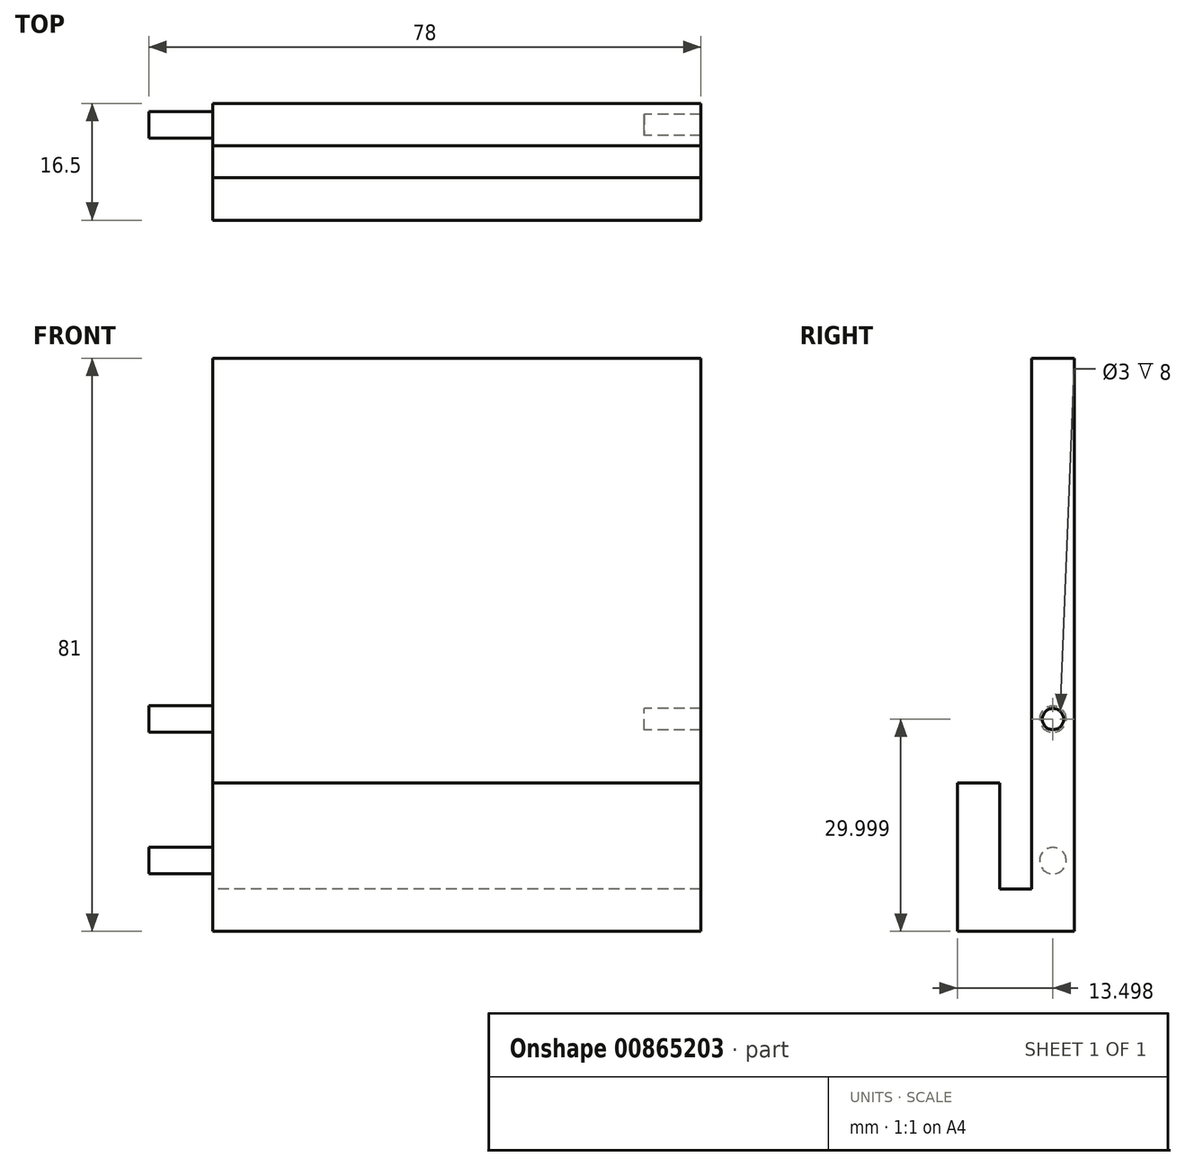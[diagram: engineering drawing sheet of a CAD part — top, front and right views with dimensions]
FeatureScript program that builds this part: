
annotation { "Feature Type Name" : "Feature", "Feature Type Description" : "" }
export const myFeature = defineFeature(function(context is Context, id is Id, definition is map)
    precondition{}
    {
        {
            var Q0;
            Q0=qCreatedBy(makeId("Right.planeOp"),FACE);
            var sketch = newSketch(context, id + "F0", { "sketchPlane" : qUnion([Q0])});
            skLineSegment(sketch, "E0", {"start": v(15.98, 53.88) * mm, "end": v(15.98, -27.12) * mm});
            skLineSegment(sketch, "E1", {"start": v(-0.52, -27.12) * mm, "end": v(15.98, -27.12) * mm});
            skLineSegment(sketch, "E2", {"start": v(-0.52, -27.12) * mm, "end": v(-0.52, -6.12) * mm});
            skLineSegment(sketch, "E3", {"start": v(5.48, -6.12) * mm, "end": v(5.48, -21.12) * mm});
            skLineSegment(sketch, "E4", {"start": v(5.48, -21.12) * mm, "end": v(9.98, -21.12) * mm});
            skLineSegment(sketch, "E5", {"start": v(9.98, -21.12) * mm, "end": v(9.98, 53.88) * mm});
            skLineSegment(sketch, "E6", {"start": v(9.98, 53.88) * mm, "end": v(15.98, 53.88) * mm});
            skLineSegment(sketch, "E7", {"start": v(-0.52, -6.12) * mm, "end": v(5.48, -6.12) * mm});
            skSolve(sketch);
        }
        {
            var Q0;
            Q0=makeQuery(id+"F0.imprint","IMPRINT",FACE,{"disambiguationData":[TD([[makeQuery(id+"F0.imprint","IMPRINT",EDGE,{"derivedFrom":sQuery(id+"F0.wireOp",EDGE,"E0")}),-1.0]])]});
            extrude(context, id + "F1", {"entities" : qUnion([Q0]), "depth" : 70 * mm, "offsetDistance" : 25 * mm});
        }
        {
            var Q0;
            Q0=makeQuery(id+"F1.opExtrude","CAP_FACE",FACE,{"disambiguationData":[OSD([sQuery(id+"F0.wireOp",EDGE,"E0"),sQuery(id+"F0.wireOp",EDGE,"E1"),sQuery(id+"F0.wireOp",EDGE,"E2"),sQuery(id+"F0.wireOp",EDGE,"E3"),sQuery(id+"F0.wireOp",EDGE,"E4"),sQuery(id+"F0.wireOp",EDGE,"E5"),sQuery(id+"F0.wireOp",EDGE,"E6"),sQuery(id+"F0.wireOp",EDGE,"E7")])],"isStart":false});
            var sketch = newSketch(context, id + "F2", { "sketchPlane" : qUnion([Q0])});
            skCircle(sketch, "E8", {"center": v(12.98, 43.88) * mm, "radius": 1.5 * mm});
            skCircle(sketch, "E9", {"center": v(12.98, 23.88) * mm, "radius": 1.5 * mm});
            skCircle(sketch, "E10.MirrorC", {"center": v(12.98, 2.88) * mm, "radius": 1.5 * mm});
            skLineSegment(sketch, "E11", {"start": v(12.98, 43.88) * mm, "end": v(12.98, 53.88) * mm});
            skLineSegment(sketch, "E12", {"start": v(12.98, 43.88) * mm, "end": v(12.98, 23.88) * mm});
            skLineSegment(sketch, "E13", {"start": v(12.98, 23.88) * mm, "end": v(12.98, 2.88) * mm});
            skLineSegment(sketch, "E14", {"start": v(12.98, 2.88) * mm, "end": v(12.98, -17.12) * mm});
            skCircle(sketch, "E15", {"center": v(12.98, -17.12) * mm, "radius": 1.5 * mm});
            skSolve(sketch);
        }
        {
            var Q0;
            {var subQ0=sQuery(id+"F2.wireOp",EDGE,"E11");var subQ1=sQuery(id+"F2.wireOp",EDGE,"E8");var subQ2=makeQuery(id+"F2.imprint","INTERSECT",VERTEX,{"derivedFrom":[subQ1,subQ0]});Q0=makeQuery(id+"F2.imprint","IMPRINT",FACE,{"disambiguationData":[TD([[makeQuery(id+"F2.imprint","IMPRINT",EDGE,{"disambiguationData":[TD([[subQ2,1.0]])],"derivedFrom":subQ1}),1.0]])]});}
            var Q1;
            {var subQ0=sQuery(id+"F2.wireOp",EDGE,"E11");var subQ1=sQuery(id+"F2.wireOp",EDGE,"E8");var subQ2=makeQuery(id+"F2.imprint","INTERSECT",VERTEX,{"derivedFrom":[subQ1,subQ0]});Q1=makeQuery(id+"F2.imprint","IMPRINT",FACE,{"disambiguationData":[TD([[makeQuery(id+"F2.imprint","IMPRINT",EDGE,{"disambiguationData":[TD([[subQ2,-1.0]])],"derivedFrom":subQ1}),1.0]])]});}
            var Q2;
            {var subQ0=sQuery(id+"F2.wireOp",EDGE,"E12");var subQ1=sQuery(id+"F2.wireOp",EDGE,"E9");var subQ2=makeQuery(id+"F2.imprint","INTERSECT",VERTEX,{"derivedFrom":[subQ1,subQ0]});Q2=makeQuery(id+"F2.imprint","IMPRINT",FACE,{"disambiguationData":[TD([[makeQuery(id+"F2.imprint","IMPRINT",EDGE,{"disambiguationData":[TD([[subQ2,1.0]])],"derivedFrom":subQ1}),1.0]])]});}
            var Q3;
            {var subQ0=sQuery(id+"F2.wireOp",EDGE,"E12");var subQ1=sQuery(id+"F2.wireOp",EDGE,"E9");var subQ2=makeQuery(id+"F2.imprint","INTERSECT",VERTEX,{"derivedFrom":[subQ1,subQ0]});Q3=makeQuery(id+"F2.imprint","IMPRINT",FACE,{"disambiguationData":[TD([[makeQuery(id+"F2.imprint","IMPRINT",EDGE,{"disambiguationData":[TD([[subQ2,-1.0]])],"derivedFrom":subQ1}),1.0]])]});}
            var Q4;
            {var subQ0=sQuery(id+"F2.wireOp",EDGE,"E13");var subQ1=sQuery(id+"F2.wireOp",EDGE,"E10.MirrorC");var subQ2=makeQuery(id+"F2.imprint","INTERSECT",VERTEX,{"derivedFrom":[subQ1,subQ0]});Q4=makeQuery(id+"F2.imprint","IMPRINT",FACE,{"disambiguationData":[TD([[makeQuery(id+"F2.imprint","IMPRINT",EDGE,{"disambiguationData":[TD([[subQ2,-1.0]])],"derivedFrom":subQ1}),-1.0]])]});}
            var Q5;
            {var subQ0=sQuery(id+"F2.wireOp",EDGE,"E13");var subQ1=sQuery(id+"F2.wireOp",EDGE,"E10.MirrorC");var subQ2=makeQuery(id+"F2.imprint","INTERSECT",VERTEX,{"derivedFrom":[subQ1,subQ0]});Q5=makeQuery(id+"F2.imprint","IMPRINT",FACE,{"disambiguationData":[TD([[makeQuery(id+"F2.imprint","IMPRINT",EDGE,{"disambiguationData":[TD([[subQ2,1.0]])],"derivedFrom":subQ1}),-1.0]])]});}
            var Q6;
            Q6=makeQuery(id+"F2.imprint","IMPRINT",FACE,{"disambiguationData":[TD([[makeQuery(id+"F2.imprint","IMPRINT",EDGE,{"derivedFrom":sQuery(id+"F2.wireOp",EDGE,"E15")}),1.0]])]});
            extrude(context, id + "F3", {"entities" : qUnion([Q0, Q1, Q2, Q3, Q4, Q5, Q6]), "operationType" : NewBodyOperationType.ADD, "depth" : 8 * mm, "offsetDistance" : 25 * mm});
        }
        {
            var Q0;
            Q0=makeQuery(id+"F1.opExtrude","CAP_FACE",FACE,{"disambiguationData":[OSD([sQuery(id+"F0.wireOp",EDGE,"E0"),sQuery(id+"F0.wireOp",EDGE,"E1"),sQuery(id+"F0.wireOp",EDGE,"E2"),sQuery(id+"F0.wireOp",EDGE,"E3"),sQuery(id+"F0.wireOp",EDGE,"E4"),sQuery(id+"F0.wireOp",EDGE,"E5"),sQuery(id+"F0.wireOp",EDGE,"E6"),sQuery(id+"F0.wireOp",EDGE,"E7")])],"isStart":true});
            var sketch = newSketch(context, id + "F4", { "sketchPlane" : qUnion([Q0])});
            skCircle(sketch, "E16", {"center": v(-12.98, 43.88) * mm, "radius": 1.88 * mm});
            skCircle(sketch, "E17", {"center": v(-12.98, 23.88) * mm, "radius": 1.88 * mm});
            skCircle(sketch, "E18.MirrorC", {"center": v(-12.98, -17.12) * mm, "radius": 1.88 * mm});
            skCircle(sketch, "E19.MirrorC", {"center": v(-12.98, 2.88) * mm, "radius": 1.88 * mm});
            skLineSegment(sketch, "E20", {"start": v(-12.98, 53.88) * mm, "end": v(-12.98, 43.88) * mm});
            skLineSegment(sketch, "E21", {"start": v(-12.98, 43.88) * mm, "end": v(-12.98, 23.88) * mm});
            skLineSegment(sketch, "E22", {"start": v(-12.98, 23.88) * mm, "end": v(-12.98, 2.88) * mm});
            skLineSegment(sketch, "E23", {"start": v(-12.98, 2.88) * mm, "end": v(-12.98, -17.12) * mm});
            skLineSegment(sketch, "E24", {"start": v(-12.98, -17.12) * mm, "end": v(-12.98, -27.12) * mm});
            skSolve(sketch);
        }
        {
            var Q0;
            {var subQ0=sQuery(id+"F4.wireOp",EDGE,"E20");var subQ1=sQuery(id+"F4.wireOp",EDGE,"E16");var subQ2=makeQuery(id+"F4.imprint","INTERSECT",VERTEX,{"derivedFrom":[subQ1,subQ0]});Q0=makeQuery(id+"F4.imprint","IMPRINT",FACE,{"disambiguationData":[TD([[makeQuery(id+"F4.imprint","IMPRINT",EDGE,{"disambiguationData":[TD([[subQ2,1.0]])],"derivedFrom":subQ1}),1.0]])]});}
            var Q1;
            {var subQ0=sQuery(id+"F4.wireOp",EDGE,"E20");var subQ1=sQuery(id+"F4.wireOp",EDGE,"E16");var subQ2=makeQuery(id+"F4.imprint","INTERSECT",VERTEX,{"derivedFrom":[subQ1,subQ0]});Q1=makeQuery(id+"F4.imprint","IMPRINT",FACE,{"disambiguationData":[TD([[makeQuery(id+"F4.imprint","IMPRINT",EDGE,{"disambiguationData":[TD([[subQ2,-1.0]])],"derivedFrom":subQ1}),1.0]])]});}
            var Q2;
            {var subQ0=sQuery(id+"F4.wireOp",EDGE,"E21");var subQ1=sQuery(id+"F4.wireOp",EDGE,"E17");var subQ2=makeQuery(id+"F4.imprint","INTERSECT",VERTEX,{"derivedFrom":[subQ1,subQ0]});Q2=makeQuery(id+"F4.imprint","IMPRINT",FACE,{"disambiguationData":[TD([[makeQuery(id+"F4.imprint","IMPRINT",EDGE,{"disambiguationData":[TD([[subQ2,1.0]])],"derivedFrom":subQ1}),1.0]])]});}
            var Q3;
            {var subQ0=sQuery(id+"F4.wireOp",EDGE,"E21");var subQ1=sQuery(id+"F4.wireOp",EDGE,"E17");var subQ2=makeQuery(id+"F4.imprint","INTERSECT",VERTEX,{"derivedFrom":[subQ1,subQ0]});Q3=makeQuery(id+"F4.imprint","IMPRINT",FACE,{"disambiguationData":[TD([[makeQuery(id+"F4.imprint","IMPRINT",EDGE,{"disambiguationData":[TD([[subQ2,-1.0]])],"derivedFrom":subQ1}),1.0]])]});}
            var Q4;
            {var subQ0=sQuery(id+"F4.wireOp",EDGE,"E22");var subQ1=sQuery(id+"F4.wireOp",EDGE,"E19.MirrorC");var subQ2=makeQuery(id+"F4.imprint","INTERSECT",VERTEX,{"derivedFrom":[subQ1,subQ0]});Q4=makeQuery(id+"F4.imprint","IMPRINT",FACE,{"disambiguationData":[TD([[makeQuery(id+"F4.imprint","IMPRINT",EDGE,{"disambiguationData":[TD([[subQ2,-1.0]])],"derivedFrom":subQ1}),-1.0]])]});}
            var Q5;
            {var subQ0=sQuery(id+"F4.wireOp",EDGE,"E22");var subQ1=sQuery(id+"F4.wireOp",EDGE,"E19.MirrorC");var subQ2=makeQuery(id+"F4.imprint","INTERSECT",VERTEX,{"derivedFrom":[subQ1,subQ0]});Q5=makeQuery(id+"F4.imprint","IMPRINT",FACE,{"disambiguationData":[TD([[makeQuery(id+"F4.imprint","IMPRINT",EDGE,{"disambiguationData":[TD([[subQ2,1.0]])],"derivedFrom":subQ1}),-1.0]])]});}
            var Q6;
            {var subQ0=sQuery(id+"F4.wireOp",EDGE,"E23");var subQ1=sQuery(id+"F4.wireOp",EDGE,"E18.MirrorC");var subQ2=makeQuery(id+"F4.imprint","INTERSECT",VERTEX,{"derivedFrom":[subQ1,subQ0]});Q6=makeQuery(id+"F4.imprint","IMPRINT",FACE,{"disambiguationData":[TD([[makeQuery(id+"F4.imprint","IMPRINT",EDGE,{"disambiguationData":[TD([[subQ2,-1.0]])],"derivedFrom":subQ1}),-1.0]])]});}
            var Q7;
            {var subQ0=sQuery(id+"F4.wireOp",EDGE,"E23");var subQ1=sQuery(id+"F4.wireOp",EDGE,"E18.MirrorC");var subQ2=makeQuery(id+"F4.imprint","INTERSECT",VERTEX,{"derivedFrom":[subQ1,subQ0]});Q7=makeQuery(id+"F4.imprint","IMPRINT",FACE,{"disambiguationData":[TD([[makeQuery(id+"F4.imprint","IMPRINT",EDGE,{"disambiguationData":[TD([[subQ2,1.0]])],"derivedFrom":subQ1}),-1.0]])]});}
            extrude(context, id + "F5", {"entities" : qUnion([Q0, Q1, Q2, Q3, Q4, Q5, Q6, Q7]), "operationType" : NewBodyOperationType.REMOVE, "oppositeDirection" : true, "depth" : 9 * mm, "offsetDistance" : 25 * mm});
        }
    });
